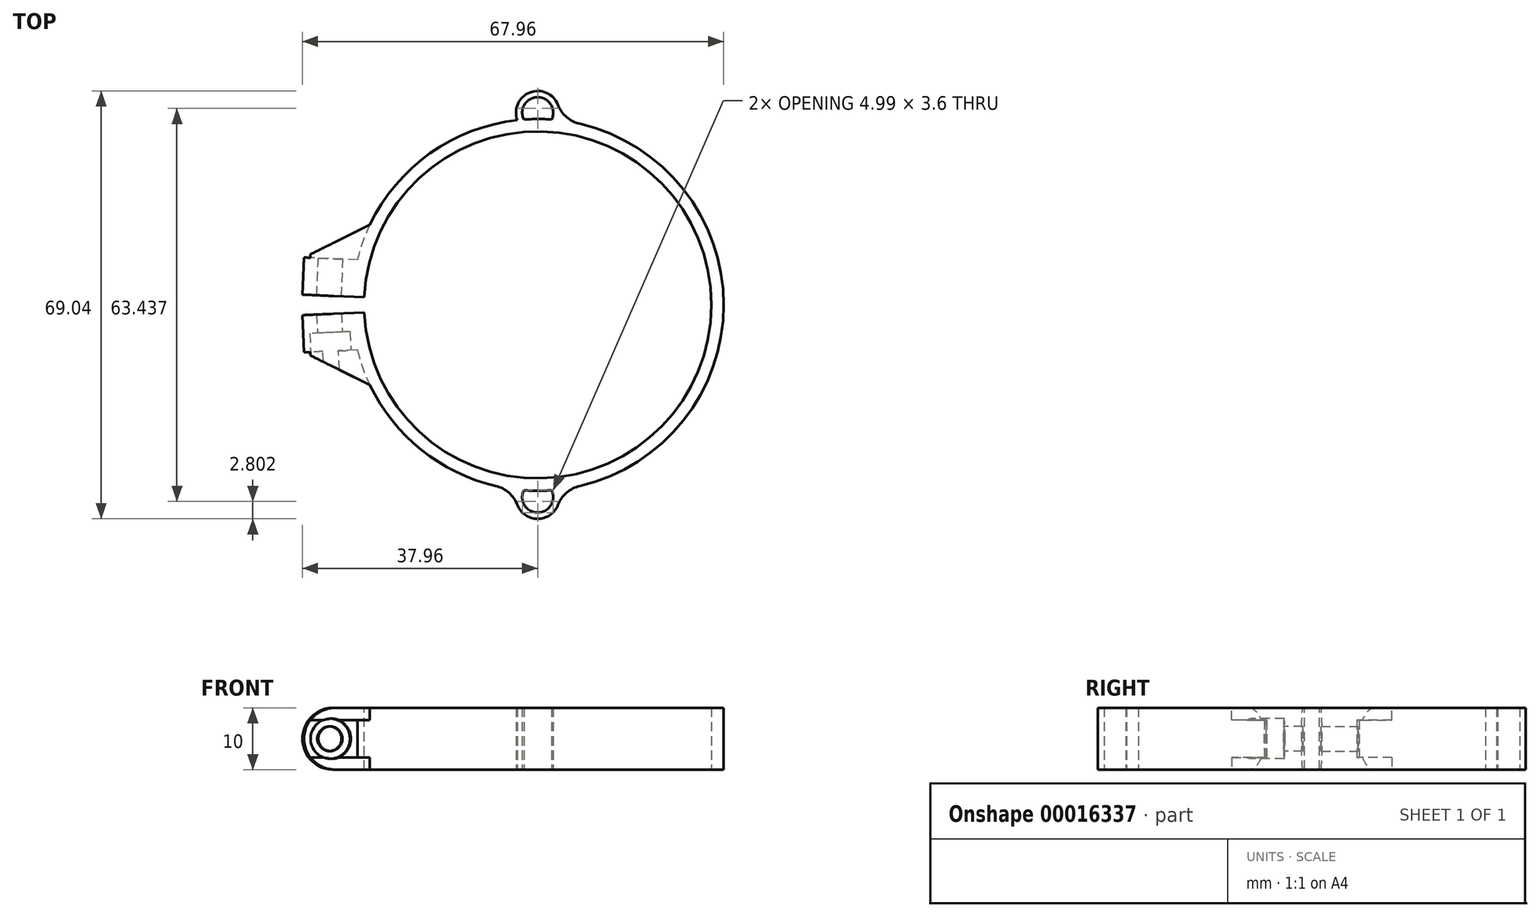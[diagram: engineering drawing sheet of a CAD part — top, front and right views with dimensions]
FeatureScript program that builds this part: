
annotation { "Feature Type Name" : "Feature", "Feature Type Description" : "" }
export const myFeature = defineFeature(function(context is Context, id is Id, definition is map)
    precondition{}
    {
        {
            var Q0;
            Q0=qCreatedBy(makeId("Top.planeOp"),FACE);
            var sketch = newSketch(context, id + "F0", { "sketchPlane" : qUnion([Q0])});
            skCircle(sketch, "E0", {"center": v(0, 0) * mm, "radius": 28 * mm});
            skCircle(sketch, "E1", {"center": v(0, 0) * mm, "radius": 30 * mm});
            skSolve(sketch);
        }
        {
            var Q0;
            Q0=makeQuery(id+"F0.imprint","IMPRINT",FACE,{"disambiguationData":[TD([[makeQuery(id+"F0.imprint","IMPRINT",EDGE,{"derivedFrom":sQuery(id+"F0.wireOp",EDGE,"E0")}),-1.0]])]});
            extrude(context, id + "F1", {"entities" : qUnion([Q0]), "depth" : 10 * mm});
        }
        {
            var Q0;
            Q0=makeQuery(id+"F1.opExtrude","CAP_FACE",FACE,{"disambiguationData":[OSD([sQuery(id+"F0.wireOp",EDGE,"E0"),sQuery(id+"F0.wireOp",EDGE,"E1")])],"isStart":false});
            var sketch = newSketch(context, id + "F2", { "sketchPlane" : qUnion([Q0])});
            skLineSegment(sketch, "E2", {"start": v(0, 0) * mm, "end": v(-27.97, -1.22) * mm});
            skLineSegment(sketch, "E3", {"start": v(-27.97, -1.22) * mm, "end": v(-29.97, -1.3) * mm});
            skLineSegment(sketch, "E4", {"start": v(0, 0) * mm, "end": v(-27.97, 1.22) * mm});
            skLineSegment(sketch, "E5", {"start": v(-27.97, 1.22) * mm, "end": v(-29.97, 1.3) * mm});
            skSolve(sketch);
        }
        {
            var Q0;
            {var subQ2=sQuery(id+"F2.wireOp",EDGE,"E3");Q0=makeQuery(id+"F2.imprint","IMPRINT",FACE,{"disambiguationData":[TD([[makeQuery(id+"F2.imprint","IMPRINT",EDGE,{"derivedFrom":subQ2}),-1.0]])]});}
            extrude(context, id + "F3", {"entities" : qUnion([Q0]), "operationType" : NewBodyOperationType.REMOVE, "endBound" : BoundingType.THROUGH_ALL, "oppositeDirection" : true, "depth" : 25 * mm});
        }
        {
            var Q0;
            Q0=makeQuery(id+"F3.boolean.opBoolean","COPY",FACE,{"derivedFrom":makeQuery(id+"F3.opExtrude","SWEPT_FACE",FACE,{"disambiguationData":[OSD([sQuery(id+"F2.wireOp",EDGE,"E5")])]})});
            var sketch = newSketch(context, id + "F4", { "sketchPlane" : qUnion([Q0])});
            skLineSegment(sketch, "E6.bottom", {"start": v(-28, 0) * mm, "end": v(-38, 0) * mm});
            skLineSegment(sketch, "E6.top", {"start": v(-28, 10) * mm, "end": v(-38, 10) * mm});
            skLineSegment(sketch, "E6.left", {"start": v(-28, 0) * mm, "end": v(-28, 10) * mm});
            skLineSegment(sketch, "E6.right", {"start": v(-38, 0) * mm, "end": v(-38, 10) * mm});
            skSolve(sketch);
        }
        {
            var Q0;
            {var subQ1=sQuery(id+"F4.wireOp",EDGE,"E6.right");Q0=makeQuery(id+"F4.imprint","IMPRINT",FACE,{"disambiguationData":[TD([[makeQuery(id+"F4.imprint","IMPRINT",EDGE,{"derivedFrom":subQ1}),-1.0]])]});}
            var Q1;
            {var subQ1=sQuery(id+"F4.wireOp",EDGE,"E6.left");Q1=makeQuery(id+"F4.imprint","IMPRINT",FACE,{"disambiguationData":[TD([[makeQuery(id+"F4.imprint","IMPRINT",EDGE,{"derivedFrom":subQ1}),1.0]])]});}
            extrude(context, id + "F5", {"entities" : qUnion([Q0, Q1]), "operationType" : NewBodyOperationType.ADD, "oppositeDirection" : true, "depth" : 6 * mm});
        }
        {
            var Q0;
            Q0=makeQuery(id+"F3.boolean.opBoolean","COPY",FACE,{"derivedFrom":makeQuery(id+"F3.opExtrude","SWEPT_FACE",FACE,{"disambiguationData":[OSD([sQuery(id+"F2.wireOp",EDGE,"E3")])]})});
            var sketch = newSketch(context, id + "F6", { "sketchPlane" : qUnion([Q0])});
            skLineSegment(sketch, "E7.bottom", {"start": v(28, 0) * mm, "end": v(38, 0) * mm});
            skLineSegment(sketch, "E7.top", {"start": v(28, 10) * mm, "end": v(38, 10) * mm});
            skLineSegment(sketch, "E7.left", {"start": v(28, 0) * mm, "end": v(28, 10) * mm});
            skLineSegment(sketch, "E7.right", {"start": v(38, 0) * mm, "end": v(38, 10) * mm});
            skSolve(sketch);
        }
        {
            var Q0;
            {var subQ1=sQuery(id+"F6.wireOp",EDGE,"E7.right");Q0=makeQuery(id+"F6.imprint","IMPRINT",FACE,{"disambiguationData":[TD([[makeQuery(id+"F6.imprint","IMPRINT",EDGE,{"derivedFrom":subQ1}),1.0]])]});}
            var Q1;
            {var subQ1=sQuery(id+"F6.wireOp",EDGE,"E7.left");Q1=makeQuery(id+"F6.imprint","IMPRINT",FACE,{"disambiguationData":[TD([[makeQuery(id+"F6.imprint","IMPRINT",EDGE,{"derivedFrom":subQ1}),-1.0]])]});}
            extrude(context, id + "F7", {"entities" : qUnion([Q0, Q1]), "operationType" : NewBodyOperationType.ADD, "oppositeDirection" : true, "depth" : 6 * mm});
        }
        {
            var Q0;
            Q0=makeQuery(id+"F5.opExtrude","CAP_FACE",FACE,{"disambiguationData":[OSD([sQuery(id+"F4.wireOp",EDGE,"E6.bottom"),sQuery(id+"F4.wireOp",EDGE,"E6.top"),sQuery(id+"F4.wireOp",EDGE,"E6.left"),sQuery(id+"F4.wireOp",EDGE,"E6.right")])],"isStart":false});
            var sketch = newSketch(context, id + "F8", { "sketchPlane" : qUnion([Q0])});
            skLineSegment(sketch, "E8", {"start": v(38, 5) * mm, "end": v(32.8, 5) * mm, "construction": true});
            skLineSegment(sketch, "E9", {"start": v(33.7, 0) * mm, "end": v(33.7, 5) * mm, "construction": true});
            skCircle(sketch, "E10", {"center": v(33.7, 5) * mm, "radius": 2 * mm});
            skCircle(sketch, "E11.cCircle", {"center": v(33.7, 5) * mm, "radius": 2 * mm, "construction": true});
            skLineSegment(sketch, "E11.0", {"start": v(35.7, 6.15) * mm, "end": v(35.7, 3.85) * mm});
            skLineSegment(sketch, "E11.1", {"start": v(35.7, 3.85) * mm, "end": v(33.7, 2.7) * mm});
            skLineSegment(sketch, "E11.2", {"start": v(33.7, 2.7) * mm, "end": v(31.7, 3.85) * mm});
            skLineSegment(sketch, "E11.3", {"start": v(31.7, 3.85) * mm, "end": v(31.7, 6.15) * mm});
            skLineSegment(sketch, "E11.4", {"start": v(31.7, 6.15) * mm, "end": v(33.7, 7.3) * mm});
            skLineSegment(sketch, "E11.5", {"start": v(33.7, 7.3) * mm, "end": v(35.7, 6.15) * mm});
            skPoint(sketch, "E11.0.midPoint", {"position": v(35.7, 5) * mm});
            skSolve(sketch);
        }
        {
            var Q0;
            Q0=makeQuery(id+"F8.imprint","IMPRINT",FACE,{"disambiguationData":[TD([[makeQuery(id+"F8.imprint","IMPRINT",EDGE,{"derivedFrom":sQuery(id+"F8.wireOp",EDGE,"E10")}),1.0]])]});
            var Q1;
            Q1=makeQuery(id+"F5.boolean.opBoolean","MERGE",FACE,{"derivedFrom":[makeQuery(id+"F3.boolean.opBoolean","COPY",FACE,{"derivedFrom":makeQuery(id+"F3.opExtrude","SWEPT_FACE",FACE,{"disambiguationData":[OSD([sQuery(id+"F2.wireOp",EDGE,"E5")])]})}),makeQuery(id+"F5.opExtrude","CAP_FACE",FACE,{"disambiguationData":[OSD([sQuery(id+"F4.wireOp",EDGE,"E6.bottom"),sQuery(id+"F4.wireOp",EDGE,"E6.top"),sQuery(id+"F4.wireOp",EDGE,"E6.left"),sQuery(id+"F4.wireOp",EDGE,"E6.right")])],"isStart":true})]});
            extrude(context, id + "F9", {"entities" : qUnion([Q0]), "operationType" : NewBodyOperationType.REMOVE, "endBound" : BoundingType.UP_TO_SURFACE, "oppositeDirection" : true, "endBoundEntityFace" : qUnion([Q1]), "depth" : 4 * mm});
        }
        {
            var Q0;
            Q0=makeQuery(id+"F7.opExtrude","CAP_FACE",FACE,{"disambiguationData":[OSD([sQuery(id+"F6.wireOp",EDGE,"E7.bottom"),sQuery(id+"F6.wireOp",EDGE,"E7.top"),sQuery(id+"F6.wireOp",EDGE,"E7.left"),sQuery(id+"F6.wireOp",EDGE,"E7.right")])],"isStart":false});
            var sketch = newSketch(context, id + "F10", { "sketchPlane" : qUnion([Q0])});
            skLineSegment(sketch, "E12", {"start": v(-38, 5) * mm, "end": v(-30.7, 5) * mm, "construction": true});
            skLineSegment(sketch, "E13", {"start": v(-33.7, 10) * mm, "end": v(-33.7, 5) * mm, "construction": true});
            skCircle(sketch, "E14", {"center": v(-33.7, 5) * mm, "radius": 2 * mm});
            skCircle(sketch, "E15", {"center": v(-33.7, 5) * mm, "radius": 3.25 * mm});
            skSolve(sketch);
        }
        {
            var Q0;
            Q0=makeQuery(id+"F10.imprint","IMPRINT",FACE,{"disambiguationData":[TD([[makeQuery(id+"F10.imprint","IMPRINT",EDGE,{"derivedFrom":sQuery(id+"F10.wireOp",EDGE,"E14")}),1.0]])]});
            extrude(context, id + "F11", {"entities" : qUnion([Q0]), "operationType" : NewBodyOperationType.REMOVE, "oppositeDirection" : true, "depth" : 6 * mm});
        }
        {
            var Q0;
            Q0 = qSketchRegion(id + "F10", true);
            extrude(context, id + "F12", {"entities" : qUnion([Q0]), "operationType" : NewBodyOperationType.REMOVE, "oppositeDirection" : true, "depth" : 3 * mm});
        }
        {
            var Q0;
            Q0=makeQuery(id+"F7.boolean.opBoolean","MERGE",FACE,{"derivedFrom":[makeQuery(id+"F5.boolean.opBoolean","MERGE",FACE,{"derivedFrom":[makeQuery(id+"F1.opExtrude","CAP_FACE",FACE,{"disambiguationData":[OSD([sQuery(id+"F0.wireOp",EDGE,"E0"),sQuery(id+"F0.wireOp",EDGE,"E1")])],"isStart":false}),makeQuery(id+"F5.opExtrude","SWEPT_FACE",FACE,{"disambiguationData":[OSD([sQuery(id+"F4.wireOp",EDGE,"E6.top")])]})]}),makeQuery(id+"F7.opExtrude","SWEPT_FACE",FACE,{"disambiguationData":[OSD([sQuery(id+"F6.wireOp",EDGE,"E7.top")])]})]});
            var sketch = newSketch(context, id + "F13", { "sketchPlane" : qUnion([Q0])});
            skLineSegment(sketch, "E16", {"start": v(-37.7, 7.65) * mm, "end": v(-27.07, 12.92) * mm});
            skLineSegment(sketch, "E17", {"start": v(-27.07, 12.92) * mm, "end": v(-29.1, 7.28) * mm});
            skLineSegment(sketch, "E18", {"start": v(-29.1, 7.28) * mm, "end": v(-37.7, 7.65) * mm});
            skLineSegment(sketch, "E19.MirrorCS", {"start": v(-37.7, -7.65) * mm, "end": v(-27.07, -12.92) * mm});
            skLineSegment(sketch, "E20.MirrorCS", {"start": v(-27.07, -12.92) * mm, "end": v(-29.1, -7.28) * mm});
            skLineSegment(sketch, "E21.MirrorCS", {"start": v(-29.1, -7.28) * mm, "end": v(-37.7, -7.65) * mm});
            skSolve(sketch);
        }
        {
            var Q0;
            {var subQ1=sQuery(id+"F13.wireOp",EDGE,"E16");Q0=makeQuery(id+"F13.imprint","IMPRINT",FACE,{"disambiguationData":[TD([[makeQuery(id+"F13.imprint","IMPRINT",EDGE,{"derivedFrom":subQ1}),-1.0]])]});}
            var Q1;
            {var subQ1=sQuery(id+"F13.wireOp",EDGE,"E19.MirrorCS");Q1=makeQuery(id+"F13.imprint","IMPRINT",FACE,{"disambiguationData":[TD([[makeQuery(id+"F13.imprint","IMPRINT",EDGE,{"derivedFrom":subQ1}),1.0]])]});}
            extrude(context, id + "F14", {"entities" : qUnion([Q0, Q1]), "operationType" : NewBodyOperationType.ADD, "oppositeDirection" : true, "depth" : 2 * mm});
        }
        {
            var Q0;
            Q0=makeQuery(id+"F7.boolean.opBoolean","MERGE",FACE,{"derivedFrom":[makeQuery(id+"F5.boolean.opBoolean","MERGE",FACE,{"derivedFrom":[makeQuery(id+"F1.opExtrude","CAP_FACE",FACE,{"disambiguationData":[OSD([sQuery(id+"F0.wireOp",EDGE,"E0"),sQuery(id+"F0.wireOp",EDGE,"E1")])],"isStart":true}),makeQuery(id+"F5.opExtrude","SWEPT_FACE",FACE,{"disambiguationData":[OSD([sQuery(id+"F4.wireOp",EDGE,"E6.bottom")])]})]}),makeQuery(id+"F7.opExtrude","SWEPT_FACE",FACE,{"disambiguationData":[OSD([sQuery(id+"F6.wireOp",EDGE,"E7.bottom")])]})]});
            var sketch = newSketch(context, id + "F15", { "sketchPlane" : qUnion([Q0])});
            skLineSegment(sketch, "E22", {"start": v(-37.7, 7.65) * mm, "end": v(-29.1, 7.28) * mm});
            skLineSegment(sketch, "E23", {"start": v(-29.1, 7.28) * mm, "end": v(-27.07, 12.92) * mm});
            skLineSegment(sketch, "E24", {"start": v(-27.07, 12.92) * mm, "end": v(-37.7, 7.65) * mm});
            skLineSegment(sketch, "E25.MirrorCS", {"start": v(-37.7, -7.65) * mm, "end": v(-29.1, -7.28) * mm});
            skLineSegment(sketch, "E26.MirrorCS", {"start": v(-29.1, -7.28) * mm, "end": v(-27.07, -12.92) * mm});
            skLineSegment(sketch, "E27.MirrorCS", {"start": v(-27.07, -12.92) * mm, "end": v(-37.7, -7.65) * mm});
            skSolve(sketch);
        }
        {
            var Q0;
            {var subQ3=sQuery(id+"F15.wireOp",EDGE,"E22");Q0=makeQuery(id+"F15.imprint","IMPRINT",FACE,{"disambiguationData":[TD([[makeQuery(id+"F15.imprint","IMPRINT",EDGE,{"derivedFrom":subQ3}),-1.0]])]});}
            var Q1;
            {var subQ3=sQuery(id+"F15.wireOp",EDGE,"E25.MirrorCS");Q1=makeQuery(id+"F15.imprint","IMPRINT",FACE,{"disambiguationData":[TD([[makeQuery(id+"F15.imprint","IMPRINT",EDGE,{"derivedFrom":subQ3}),1.0]])]});}
            extrude(context, id + "F16", {"entities" : qUnion([Q0, Q1]), "operationType" : NewBodyOperationType.ADD, "oppositeDirection" : true, "depth" : 2 * mm});
        }
        {
            var Q0;
            Q0=makeQuery(id+"F12.boolean.opBoolean","COPY",FACE,{"derivedFrom":makeQuery(id+"F12.opExtrude","CAP_FACE",FACE,{"disambiguationData":[OSD([sQuery(id+"F10.wireOp",EDGE,"E14"),sQuery(id+"F10.wireOp",EDGE,"E15")])],"isStart":false})});
            extrude(context, id + "F17", {"entities" : qUnion([Q0]), "operationType" : NewBodyOperationType.REMOVE, "depth" : 25 * mm});
        }
        {
            var Q0;
            Q0=makeQuery(id+"F7.opExtrude","SWEPT_EDGE",EDGE,{"disambiguationData":[OSD([sQuery(id+"F6.wireOp",EDGE,"E7.top"),sQuery(id+"F6.wireOp",EDGE,"E7.right")])]});
            var Q1;
            Q1=makeQuery(id+"F7.opExtrude","SWEPT_EDGE",EDGE,{"disambiguationData":[OSD([sQuery(id+"F6.wireOp",EDGE,"E7.bottom"),sQuery(id+"F6.wireOp",EDGE,"E7.right")])]});
            var Q2;
            Q2=makeQuery(id+"F5.opExtrude","SWEPT_EDGE",EDGE,{"disambiguationData":[OSD([sQuery(id+"F4.wireOp",EDGE,"E6.bottom"),sQuery(id+"F4.wireOp",EDGE,"E6.right")])]});
            var Q3;
            Q3=makeQuery(id+"F5.opExtrude","SWEPT_EDGE",EDGE,{"disambiguationData":[OSD([sQuery(id+"F4.wireOp",EDGE,"E6.top"),sQuery(id+"F4.wireOp",EDGE,"E6.right")])]});
            fillet(context, id + "F18", {"entities" : qUnion([Q0, Q1, Q2, Q3]), "radius" : 5 * mm, "tangentPropagation" : true, "allowEdgeOverflow" : false});
        }
        {
            var Q0;
            {var subQ0=sQuery(id+"F0.wireOp",EDGE,"E1");Q0=makeQuery(id+"F16.boolean.opBoolean","MERGE",FACE,{"derivedFrom":[makeQuery(id+"F7.boolean.opBoolean","MERGE",FACE,{"derivedFrom":[makeQuery(id+"F5.boolean.opBoolean","MERGE",FACE,{"derivedFrom":[makeQuery(id+"F1.opExtrude","CAP_FACE",FACE,{"disambiguationData":[OSD([sQuery(id+"F0.wireOp",EDGE,"E0"),subQ0])],"isStart":true}),makeQuery(id+"F5.opExtrude","SWEPT_FACE",FACE,{"disambiguationData":[OSD([sQuery(id+"F4.wireOp",EDGE,"E6.bottom")])]})]}),makeQuery(id+"F7.opExtrude","SWEPT_FACE",FACE,{"disambiguationData":[OSD([sQuery(id+"F6.wireOp",EDGE,"E7.bottom")])]})]}),makeQuery(id+"F16.opExtrude","CAP_FACE",FACE,{"disambiguationData":[OSD([subQ0,sQuery(id+"F15.wireOp",EDGE,"E22"),sQuery(id+"F15.wireOp",EDGE,"E24")])],"isStart":true}),makeQuery(id+"F16.opExtrude","CAP_FACE",FACE,{"disambiguationData":[OSD([subQ0,sQuery(id+"F15.wireOp",EDGE,"E25.MirrorCS"),sQuery(id+"F15.wireOp",EDGE,"E27.MirrorCS")])],"isStart":true})]});}
            var sketch = newSketch(context, id + "F19", { "sketchPlane" : qUnion([Q0])});
            skCircle(sketch, "E28", {"center": v(0, 31.02) * mm, "radius": 2.5 * mm});
            skCircle(sketch, "E29", {"center": v(0, 31.02) * mm, "radius": 3.5 * mm});
            skCircle(sketch, "E30.1.0", {"center": v(31.02, 0) * mm, "radius": 2.5 * mm});
            skCircle(sketch, "E30.1.1", {"center": v(31.02, 0) * mm, "radius": 3.5 * mm});
            skCircle(sketch, "E30.2.0", {"center": v(0, -31.02) * mm, "radius": 2.5 * mm});
            skCircle(sketch, "E30.2.1", {"center": v(0, -31.02) * mm, "radius": 3.5 * mm});
            skPoint(sketch, "E30.center", {"position": v(0, 0) * mm});
            skLineSegment(sketch, "E30.anchor1", {"start": v(0, 0) * mm, "end": v(0, 31.02) * mm, "construction": true});
            skLineSegment(sketch, "E30.anchor2", {"start": v(0, 0) * mm, "end": v(0, -31.02) * mm, "construction": true});
            skSolve(sketch);
        }
        {
            var Q0;
            {var subQ0=makeQuery(id+"F1.opExtrude","CAP_EDGE",EDGE,{"disambiguationData":[OSD([sQuery(id+"F0.wireOp",EDGE,"E1")])],"isStart":true});var subQ1=sQuery(id+"F19.wireOp",EDGE,"E28");var subQ2=makeQuery(id+"F19.imprint","INTERSECT",VERTEX,{"disambiguationData":[OD(0.0)],"derivedFrom":[subQ0,subQ1]});Q0=makeQuery(id+"F19.imprint","IMPRINT",FACE,{"disambiguationData":[TD([[makeQuery(id+"F19.imprint","IMPRINT",EDGE,{"disambiguationData":[TD([[subQ2,1.0]])],"derivedFrom":subQ1}),-1.0]])]});}
            var Q1;
            {var subQ0=makeQuery(id+"F1.opExtrude","CAP_EDGE",EDGE,{"disambiguationData":[OSD([sQuery(id+"F0.wireOp",EDGE,"E1")])],"isStart":true});var subQ1=sQuery(id+"F19.wireOp",EDGE,"E30.2.0");var subQ5=makeQuery(id+"F19.imprint","INTERSECT",VERTEX,{"disambiguationData":[OD(0.0)],"derivedFrom":[subQ0,subQ1]});Q1=makeQuery(id+"F19.imprint","IMPRINT",FACE,{"disambiguationData":[TD([[makeQuery(id+"F19.imprint","IMPRINT",EDGE,{"disambiguationData":[TD([[subQ5,1.0]])],"derivedFrom":subQ1}),-1.0]])]});}
            var Q2;
            {var subQ0=makeQuery(id+"F1.opExtrude","CAP_EDGE",EDGE,{"disambiguationData":[OSD([sQuery(id+"F0.wireOp",EDGE,"E1")])],"isStart":true});var subQ1=sQuery(id+"F19.wireOp",EDGE,"E30.1.0");var subQ5=makeQuery(id+"F19.imprint","INTERSECT",VERTEX,{"disambiguationData":[OD(0.0)],"derivedFrom":[subQ0,subQ1]});Q2=makeQuery(id+"F19.imprint","IMPRINT",FACE,{"disambiguationData":[TD([[makeQuery(id+"F19.imprint","IMPRINT",EDGE,{"disambiguationData":[TD([[subQ5,1.0]])],"derivedFrom":subQ1}),-1.0]])]});}
            extrude(context, id + "F20", {"entities" : qUnion([Q0, Q1, Q2]), "operationType" : NewBodyOperationType.ADD, "oppositeDirection" : true, "depth" : 10 * mm});
        }
        {
            var Q0;
            {var subQ0=sQuery(id+"F0.wireOp",EDGE,"E1");var subQ1=sQuery(id+"F19.wireOp",EDGE,"E30.2.1");Q0=makeQuery(id+"F20.opExtrude","SWEPT_EDGE",EDGE,{"disambiguationData":[OSD([subQ0,subQ1]),TDD([makeQuery(id+"F19.imprint","INTERSECT",VERTEX,{"disambiguationData":[OD(1.0)],"derivedFrom":[makeQuery(id+"F1.opExtrude","CAP_EDGE",EDGE,{"disambiguationData":[OSD([subQ0])],"isStart":true}),subQ1]})])]});}
            var Q1;
            {var subQ0=sQuery(id+"F0.wireOp",EDGE,"E1");var subQ1=sQuery(id+"F19.wireOp",EDGE,"E30.2.1");Q1=makeQuery(id+"F20.opExtrude","SWEPT_EDGE",EDGE,{"disambiguationData":[OSD([subQ0,subQ1]),TDD([makeQuery(id+"F19.imprint","INTERSECT",VERTEX,{"disambiguationData":[OD(0.0)],"derivedFrom":[makeQuery(id+"F1.opExtrude","CAP_EDGE",EDGE,{"disambiguationData":[OSD([subQ0])],"isStart":true}),subQ1]})])]});}
            var Q2;
            {var subQ0=sQuery(id+"F0.wireOp",EDGE,"E1");var subQ1=sQuery(id+"F19.wireOp",EDGE,"E30.1.1");Q2=makeQuery(id+"F20.opExtrude","SWEPT_EDGE",EDGE,{"disambiguationData":[OSD([subQ0,subQ1]),TDD([makeQuery(id+"F19.imprint","INTERSECT",VERTEX,{"disambiguationData":[OD(1.0)],"derivedFrom":[makeQuery(id+"F1.opExtrude","CAP_EDGE",EDGE,{"disambiguationData":[OSD([subQ0])],"isStart":true}),subQ1]})])]});}
            var Q3;
            {var subQ0=sQuery(id+"F0.wireOp",EDGE,"E1");var subQ1=sQuery(id+"F19.wireOp",EDGE,"E30.1.1");Q3=makeQuery(id+"F20.opExtrude","SWEPT_EDGE",EDGE,{"disambiguationData":[OSD([subQ0,subQ1]),TDD([makeQuery(id+"F19.imprint","INTERSECT",VERTEX,{"disambiguationData":[OD(0.0)],"derivedFrom":[makeQuery(id+"F1.opExtrude","CAP_EDGE",EDGE,{"disambiguationData":[OSD([subQ0])],"isStart":true}),subQ1]})])]});}
            var Q4;
            {var subQ0=sQuery(id+"F0.wireOp",EDGE,"E1");var subQ1=sQuery(id+"F19.wireOp",EDGE,"E29");Q4=makeQuery(id+"F20.opExtrude","SWEPT_EDGE",EDGE,{"disambiguationData":[OSD([subQ0,subQ1]),TDD([makeQuery(id+"F19.imprint","INTERSECT",VERTEX,{"disambiguationData":[OD(1.0)],"derivedFrom":[makeQuery(id+"F1.opExtrude","CAP_EDGE",EDGE,{"disambiguationData":[OSD([subQ0])],"isStart":true}),subQ1]})])]});}
            var Q5;
            {var subQ0=sQuery(id+"F0.wireOp",EDGE,"E1");var subQ1=sQuery(id+"F19.wireOp",EDGE,"E29");Q5=makeQuery(id+"F20.opExtrude","SWEPT_EDGE",EDGE,{"disambiguationData":[OSD([subQ0,subQ1]),TDD([makeQuery(id+"F19.imprint","INTERSECT",VERTEX,{"disambiguationData":[OD(0.0)],"derivedFrom":[makeQuery(id+"F1.opExtrude","CAP_EDGE",EDGE,{"disambiguationData":[OSD([subQ0])],"isStart":true}),subQ1]})])]});}
            fillet(context, id + "F21", {"entities" : qUnion([Q0, Q1, Q2, Q3, Q4, Q5]), "radius" : 5 * mm, "tangentPropagation" : true, "allowEdgeOverflow" : false});
        }
    });
